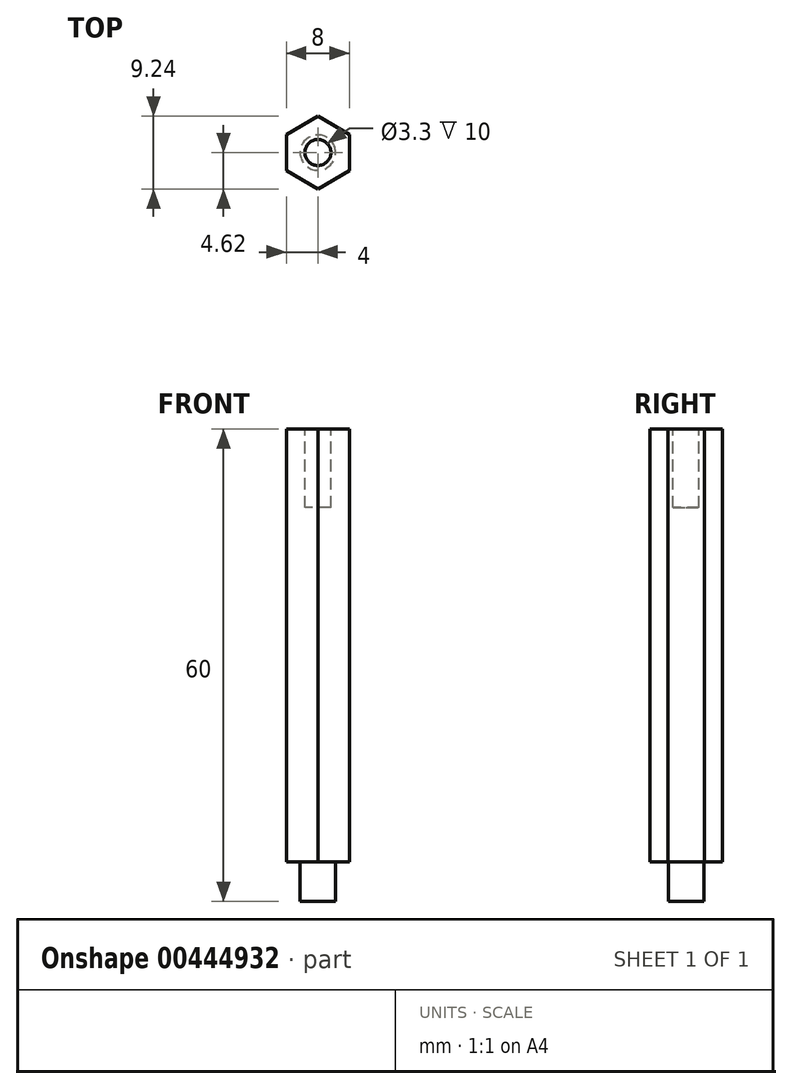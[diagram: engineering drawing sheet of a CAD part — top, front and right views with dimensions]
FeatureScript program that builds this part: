
annotation { "Feature Type Name" : "Feature", "Feature Type Description" : "" }
export const myFeature = defineFeature(function(context is Context, id is Id, definition is map)
    precondition{}
    {
        {
            var Q0;
            Q0=qCreatedBy(makeId("Top.planeOp"),FACE);
            var sketch = newSketch(context, id + "F0", { "sketchPlane" : qUnion([Q0])});
            skCircle(sketch, "E0.cCircle", {"center": v(0, 0) * mm, "radius": 4 * mm, "construction": true});
            skLineSegment(sketch, "E0.0", {"start": v(4, 2.3) * mm, "end": v(4, -2.3) * mm});
            skLineSegment(sketch, "E0.1", {"start": v(4, -2.3) * mm, "end": v(0, -4.62) * mm});
            skLineSegment(sketch, "E0.2", {"start": v(0, -4.62) * mm, "end": v(-4, -2.3) * mm});
            skLineSegment(sketch, "E0.3", {"start": v(-4, -2.3) * mm, "end": v(-4, 2.3) * mm});
            skLineSegment(sketch, "E0.4", {"start": v(-4, 2.3) * mm, "end": v(0, 4.62) * mm});
            skLineSegment(sketch, "E0.5", {"start": v(0, 4.62) * mm, "end": v(4, 2.3) * mm});
            skPoint(sketch, "E0.0.midPoint", {"position": v(4, 0) * mm});
            skCircle(sketch, "E1", {"center": v(0, 0) * mm, "radius": 2.25 * mm});
            skSolve(sketch);
        }
        {
            var Q0;
            Q0=makeQuery(id+"F0.imprint","IMPRINT",FACE,{"disambiguationData":[TD([[makeQuery(id+"F0.imprint","IMPRINT",EDGE,{"derivedFrom":sQuery(id+"F0.wireOp",EDGE,"E0.0")}),-1.0]])]});
            var Q1;
            Q1=makeQuery(id+"F0.imprint","IMPRINT",FACE,{"disambiguationData":[TD([[makeQuery(id+"F0.imprint","IMPRINT",EDGE,{"derivedFrom":sQuery(id+"F0.wireOp",EDGE,"E1")}),1.0]])]});
            extrude(context, id + "F1", {"entities" : qUnion([Q0, Q1]), "depth" : 55 * mm});
        }
        {
            var Q0;
            Q0=makeQuery(id+"F0.imprint","IMPRINT",FACE,{"disambiguationData":[TD([[makeQuery(id+"F0.imprint","IMPRINT",EDGE,{"derivedFrom":sQuery(id+"F0.wireOp",EDGE,"E1")}),1.0]])]});
            extrude(context, id + "F2", {"entities" : qUnion([Q0]), "operationType" : NewBodyOperationType.ADD, "oppositeDirection" : true, "depth" : 5 * mm});
        }
        {
            var Q0;
            Q0=makeQuery(id+"F1.opExtrude","CAP_FACE",FACE,{"disambiguationData":[OSD([sQuery(id+"F0.wireOp",EDGE,"E0.0"),sQuery(id+"F0.wireOp",EDGE,"E0.1"),sQuery(id+"F0.wireOp",EDGE,"E0.2"),sQuery(id+"F0.wireOp",EDGE,"E0.3"),sQuery(id+"F0.wireOp",EDGE,"E0.4"),sQuery(id+"F0.wireOp",EDGE,"E0.5")])],"isStart":false});
            var sketch = newSketch(context, id + "F3", { "sketchPlane" : qUnion([Q0])});
            skCircle(sketch, "E2", {"center": v(0, 0) * mm, "radius": 1.65 * mm});
            skSolve(sketch);
        }
        {
            var Q0;
            Q0=makeQuery(id+"F3.imprint","IMPRINT",FACE,{"disambiguationData":[TD([[makeQuery(id+"F3.imprint","IMPRINT",EDGE,{"derivedFrom":sQuery(id+"F3.wireOp",EDGE,"E2")}),1.0]])]});
            extrude(context, id + "F4", {"entities" : qUnion([Q0]), "operationType" : NewBodyOperationType.REMOVE, "oppositeDirection" : true, "depth" : 10 * mm});
        }
    });
